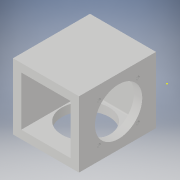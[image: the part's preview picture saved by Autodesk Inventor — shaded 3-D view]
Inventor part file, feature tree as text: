
AUTODESK INVENTOR PART (.ipt)
format: ipt  version: 2019 (Build 230136000, 136)  size: 220,672 bytes
history: native  units: in
note: dims shown in document units (in); Inventor stores cm internally (conversion verified against a paired STEP export)
features: sketch x9, extrude x4, hole x3, other x2, fillet x1
ambient origin geometry x8: Origin, YZ Plane, XZ Plane, XY Plane, X Axis, Y Axis, Z Axis, Center Point
bodies: Solid1 (feature_tree)
feature tree (19):
  sketch  "Sketch1"  dims[d0=1.7717in d1=1.7717in]
  extrude  "Extrusion1"  Depth=1.7717in
  extrude  "Extrusion2"  Depth=2.3622in
  extrude  "Extrusion4"  Depth=0.7874in TaperAngle=0.0deg
  fillet  "Fillet3"  Radius=0.7874in
  sketch  "Sketch9"  dims[d36=1.6929in d37=1.1811in]
  other  "Move Face1"
  other  "Move Face2"
  sketch  "Sketch2"  dims[d2=2.3622in d3=2.3622in]
  sketch  "Sketch3"  dims[d4=2.1654in d5=0.0in d6=0.7874in d7=0.0in d28=0.7874in d29=0.0in]
  sketch  "Sketch5"  dims[d31=0.0in d32=0.7874in d33=1.6929in]
  sketch  "Sketch10"  dims[d38=0.4331in d57=0.0394in]
  sketch  "Sketch11"  dims[d58=0.1575in]
  sketch  "Sketch12"  dims[d60=1.5748in d61=360.0deg d62=0.1969in d63=0.6959in d64=0.6959in d65=0.0in d66=90.0deg d67=0.0787in d68=0.1575in d69=0.1575in d70=0.13in d71=0.1575in d73=1.5748in d74=360.0deg d75=0.1969in d76=0.6959in d77=0.6959in d78=0.0in d79=90.0deg d80=0.0787in d81=0.1575in d82=0.1575in d83=0.13in d84=0.1378in d85=1.3197in d86=1.3197in d87=0.0in d88=90.0deg d89=0.0787in d90=0.1575in d91=0.1575in d92=0.196in d93=2.6394in d94=2.6394in d131=0.0197in d158=0.0197in d179=0.0197in]
  sketch  "Sketch6"  dims[d34=1.1811in d35=0.4331in]
  extrude  "Extrusion5"  Depth=0.7874in
  hole  "Hole5"  [1 undecoded]
  hole  "Hole3"  [1 undecoded]
  hole  "Hole4"  [1 undecoded]
note: 3 required parameter values undecoded (feature->parameter linkage not recoverable at this tier; creation-order binding heuristic only, values carry confidence <= 0.55)
